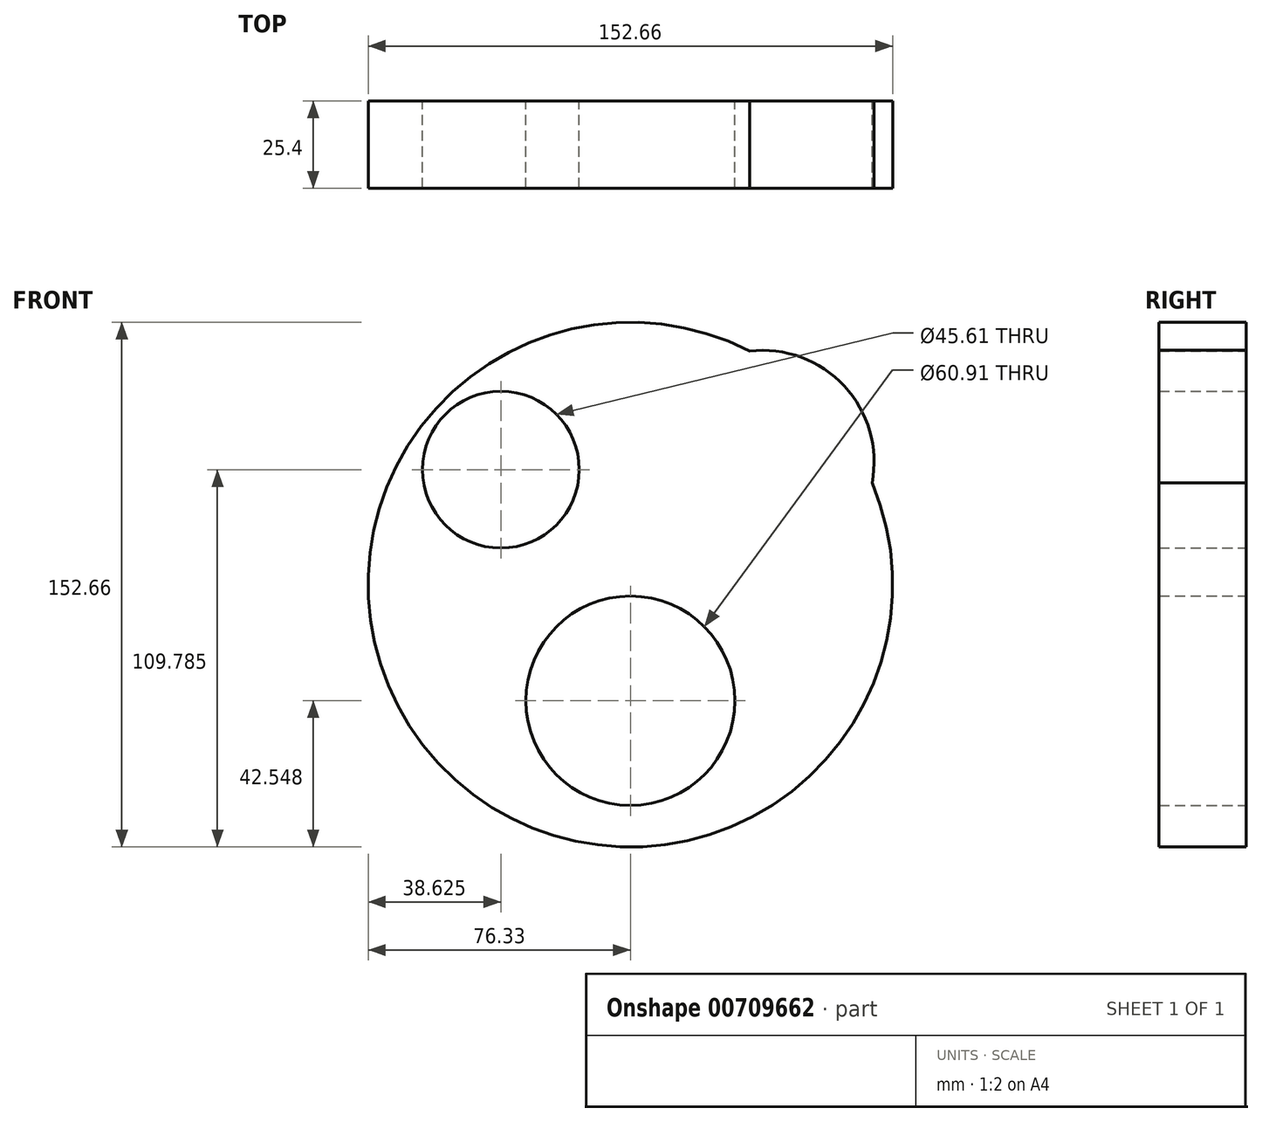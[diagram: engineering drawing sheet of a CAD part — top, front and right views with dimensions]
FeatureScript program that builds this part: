
annotation { "Feature Type Name" : "Feature", "Feature Type Description" : "" }
export const myFeature = defineFeature(function(context is Context, id is Id, definition is map)
    precondition{}
    {
        {
            var Q0;
            Q0=qCreatedBy(makeId("Front.planeOp"),FACE);
            var sketch = newSketch(context, id + "F0", { "sketchPlane" : qUnion([Q0])});
            skCircle(sketch, "E0", {"center": v(0, 0) * mm, "radius": 76.33 * mm});
            skCircle(sketch, "E1", {"center": v(-37.7, 33.46) * mm, "radius": 22.8 * mm});
            skCircle(sketch, "E2", {"center": v(38.45, 35.68) * mm, "radius": 32.5 * mm});
            skCircle(sketch, "E3", {"center": v(0, -33.78) * mm, "radius": 30.45 * mm});
            skCircle(sketch, "E4", {"center": v(0, -33.78) * mm, "radius": 16.43 * mm});
            skSolve(sketch);
        }
        {
            var Q0;
            Q0 = qSketchRegion(id + "F0", true);
            extrude(context, id + "F1", {"entities" : qUnion([Q0]), "depth" : 25.4 * mm, "offsetDistance" : 25.4 * mm});
        }
    });
